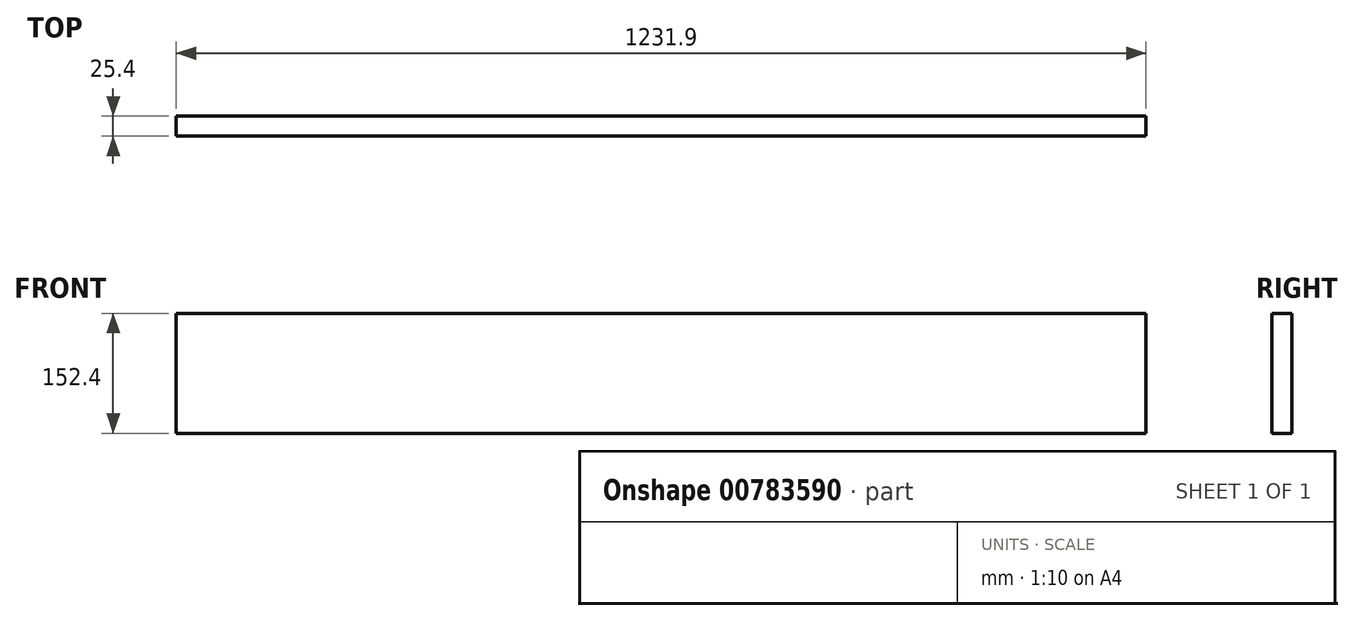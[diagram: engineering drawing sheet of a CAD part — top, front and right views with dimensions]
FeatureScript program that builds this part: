
annotation { "Feature Type Name" : "Feature", "Feature Type Description" : "" }
export const myFeature = defineFeature(function(context is Context, id is Id, definition is map)
    precondition{}
    {
        {
            var Q0;
            Q0=qCreatedBy(makeId("Front.planeOp"),FACE);
            var sketch = newSketch(context, id + "F0", { "sketchPlane" : qUnion([Q0])});
            skLineSegment(sketch, "E0.bottom", {"start": v(0, 0) * mm, "end": v(1231.9, 0) * mm});
            skLineSegment(sketch, "E0.top", {"start": v(0, 152.4) * mm, "end": v(1231.9, 152.4) * mm});
            skLineSegment(sketch, "E0.left", {"start": v(0, 0) * mm, "end": v(0, 152.4) * mm});
            skLineSegment(sketch, "E0.right", {"start": v(1231.9, 0) * mm, "end": v(1231.9, 152.4) * mm});
            skSolve(sketch);
        }
        {
            var Q0;
            Q0=makeQuery(id+"F0.imprint","IMPRINT",FACE,{"disambiguationData":[TD([[makeQuery(id+"F0.imprint","IMPRINT",EDGE,{"derivedFrom":sQuery(id+"F0.wireOp",EDGE,"E0.bottom")}),1.0]])]});
            extrude(context, id + "F1", {"entities" : qUnion([Q0]), "depth" : 25.4 * mm, "offsetDistance" : 25.4 * mm});
        }
    });
